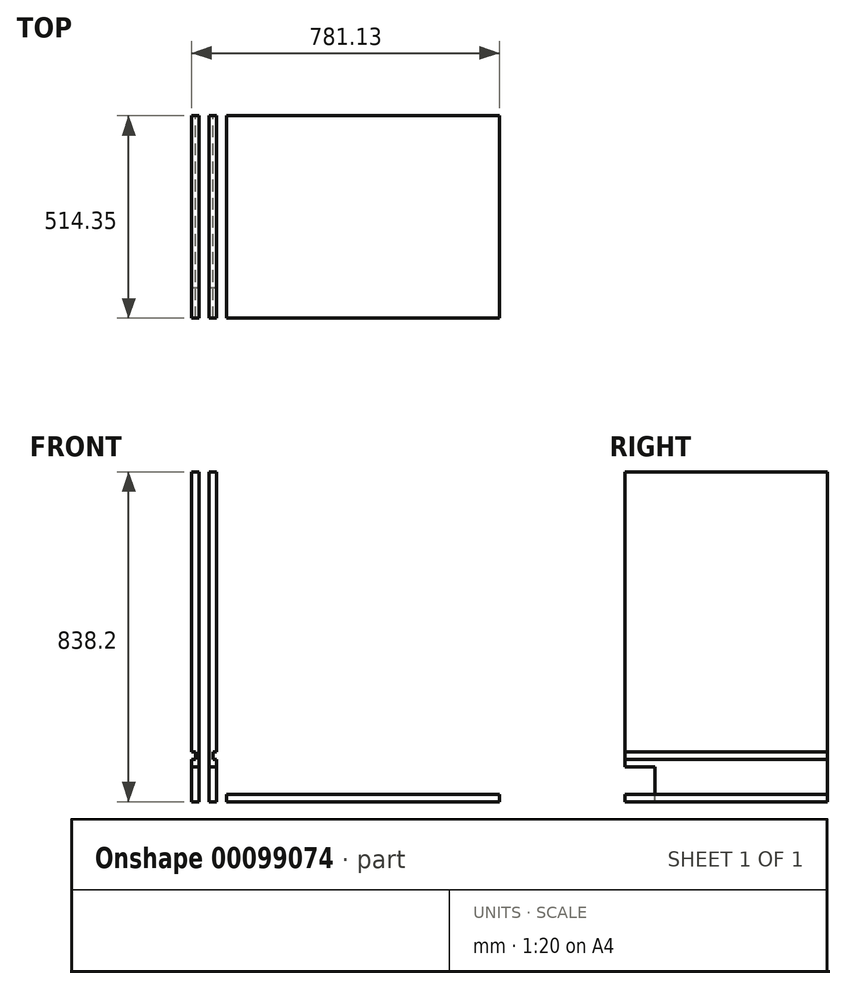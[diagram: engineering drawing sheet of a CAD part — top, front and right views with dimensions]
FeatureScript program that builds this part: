
annotation { "Feature Type Name" : "Feature", "Feature Type Description" : "" }
export const myFeature = defineFeature(function(context is Context, id is Id, definition is map)
    precondition{}
    {
        {
            var Q0;
            Q0=qCreatedBy(makeId("Front.planeOp"),FACE);
            var sketch = newSketch(context, id + "F0", { "sketchPlane" : qUnion([Q0])});
            skLineSegment(sketch, "E0.bottom", {"start": v(0, 0) * mm, "end": v(19.05, 0) * mm});
            skLineSegment(sketch, "E0.top", {"start": v(0, 838.2) * mm, "end": v(19.05, 838.2) * mm});
            skLineSegment(sketch, "E0.left", {"start": v(0, 0) * mm, "end": v(0, 838.2) * mm});
            skLineSegment(sketch, "E0.right", {"start": v(19.05, 0) * mm, "end": v(19.05, 107.95) * mm});
            skLineSegment(sketch, "E1", {"start": v(19.05, 127) * mm, "end": v(9.52, 127) * mm});
            skLineSegment(sketch, "E2", {"start": v(9.52, 127) * mm, "end": v(9.52, 107.95) * mm});
            skLineSegment(sketch, "E3", {"start": v(9.53, 107.95) * mm, "end": v(19.05, 107.95) * mm});
            skLineSegment(sketch, "E4.trimOffspring", {"start": v(19.05, 127) * mm, "end": v(19.05, 838.2) * mm});
            skLineSegment(sketch, "E5", {"start": v(-12.7, 0) * mm, "end": v(-12.7, 34.09) * mm});
            skLineSegment(sketch, "E6.MirrorCS", {"start": v(-25.4, 0) * mm, "end": v(-25.4, 838.2) * mm});
            skLineSegment(sketch, "E7.MirrorCS", {"start": v(-25.4, 0) * mm, "end": v(-44.45, 0) * mm});
            skLineSegment(sketch, "E8.MirrorCS", {"start": v(-44.45, 0) * mm, "end": v(-44.45, 107.95) * mm});
            skLineSegment(sketch, "E9.MirrorCS", {"start": v(-34.93, 107.95) * mm, "end": v(-44.45, 107.95) * mm});
            skLineSegment(sketch, "E10.MirrorCS", {"start": v(-34.93, 127) * mm, "end": v(-34.93, 107.95) * mm});
            skLineSegment(sketch, "E11.MirrorCS", {"start": v(-44.45, 127) * mm, "end": v(-44.45, 838.2) * mm});
            skLineSegment(sketch, "E12.MirrorCS", {"start": v(-44.45, 127) * mm, "end": v(-34.93, 127) * mm});
            skLineSegment(sketch, "E13.MirrorCS", {"start": v(-25.4, 838.2) * mm, "end": v(-44.45, 838.2) * mm});
            skSolve(sketch);
        }
        {
            var Q0;
            Q0 = qSketchRegion(id + "F0", true);
            extrude(context, id + "F1", {"entities" : qUnion([Q0]), "depth" : 514.35 * mm});
        }
        {
            var Q0;
            Q0=qCreatedBy(makeId("Front.planeOp"),FACE);
            var sketch = newSketch(context, id + "F2", { "sketchPlane" : qUnion([Q0])});
            skLineSegment(sketch, "E14.bottom", {"start": v(736.68, 0) * mm, "end": v(44.53, 0) * mm});
            skLineSegment(sketch, "E14.top", {"start": v(736.68, 19.05) * mm, "end": v(44.53, 19.05) * mm});
            skLineSegment(sketch, "E14.left", {"start": v(736.68, 0) * mm, "end": v(736.68, 19.05) * mm});
            skLineSegment(sketch, "E14.right", {"start": v(44.53, 0) * mm, "end": v(44.53, 19.05) * mm});
            skSolve(sketch);
        }
        {
            var Q0;
            Q0 = qSketchRegion(id + "F2", true);
            extrude(context, id + "F3", {"entities" : qUnion([Q0]), "depth" : 514.35 * mm});
        }
        {
            var Q0;
            Q0=makeQuery(id+"F1.opExtrude","SWEPT_FACE",FACE,{"disambiguationData":[OSD([sQuery(id+"F0.wireOp",EDGE,"E8.MirrorCS")])]});
            var sketch = newSketch(context, id + "F4", { "sketchPlane" : qUnion([Q0])});
            skLineSegment(sketch, "E15.bottom", {"start": v(514.35, 0) * mm, "end": v(438.15, 0) * mm});
            skLineSegment(sketch, "E15.top", {"start": v(514.35, 88.9) * mm, "end": v(438.15, 88.9) * mm});
            skLineSegment(sketch, "E15.left", {"start": v(514.35, 0) * mm, "end": v(514.35, 88.9) * mm});
            skLineSegment(sketch, "E15.right", {"start": v(438.15, 0) * mm, "end": v(438.15, 88.9) * mm});
            skSolve(sketch);
        }
        {
            var Q0;
            Q0 = qSketchRegion(id + "F4", true);
            extrude(context, id + "F5", {"entities" : qUnion([Q0]), "operationType" : NewBodyOperationType.REMOVE, "oppositeDirection" : true, "depth" : 76.2 * mm});
        }
    });
